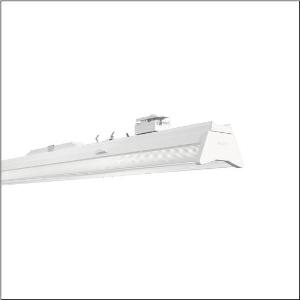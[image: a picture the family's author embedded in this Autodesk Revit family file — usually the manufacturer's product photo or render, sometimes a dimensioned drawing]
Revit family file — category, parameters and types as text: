
# Revit family: licross_r__21_performance_mo_52td167n485g_efc6
name_source: partatom
category: Lighting Fixtures
units: mm (PartAtom-declared; Revit-internal decimal feet)

## family parameters
Cut with Voids When Loaded = No
Host = Face
Light Source = No
Part Type = Normal
Room Calculation Point = No
Round Connector Dimension = Use Diameter
Shared = No

## types (1)
- Licross® 21 Performance MO (1 x LED, 8720 lm, 47.9 W, 4000K)
    Apparent Load = 48 VA
    CIE Flux Codes = 66 88 96 79 100
    Color Rendering = 80
    Color Temperature = 4000K
    Default Elevation = 1800 mm
    Description = Licross® 21 Performance MO, luminaire insert, of sheet steel, galvanised, coil coated, white, length: 1.500mm, width: 120mm, height: 123mm, LED rated luminous flux: 8.720lm, light colour: 840, SDCM (Standard Deviation of Colour Matching)MacAdam ≤ 3 SDCM (initial), control gear: ON/OFF, with plug, 3-pole, with phase selection, mains connection: 220..240V, AC, 50/60Hz, rated input power: 48W, internal wiring halogen-free, primary light control with lens, of plastic, primary optical cover: cover, of PMMA, light emission: direct/indirect distribution, primary light characteristic: symmetric, protection rating (complete): IP54, insulation class (complete): insulation class I (protective earthing), certification: CE, ENEC, UKCA, protection symbol: D if used in an environment with non-conductive dust loads with corresponding accessories, impact resistance: IK06, permissible ambient temperature for indoor applications: -35..+45°C, corresponds to IFS (International Featured Standards) requirements for safety and quality in the food industry, reducing of maximum allowable ambient temperature of 5°C with ceiling mounting, LABS conformity tested according to VDMA 24364:2018-05, packaging unit: 1 piece
    Height = 114 mm
    Lamp = 1 x LED
    Lamp Light Flux = 8720 lm
    Lamp Power = 47.9 W
    Lamp count = 1
    Length = 1500 mm
    Luminous efficacy = 182 lm/W
    Manufacturer = Siteco
    ModVariant = No
    Model = 52TD167N485G
    Mounting Place = Ceiling
    Mounting Type = Pendant
    Number of Poles = 1
    OnlyDefault = Yes
    Power Factor = 1
    Product Name = Licross® 21 Performance MO
    Product group = luminaire insert | ceiling pendant
    ProductGroupID = 901
    Protection Class = Protection class I
    Protection Degree = IP 54
    RLX_Detail_Level = 1
    RLX_Emergency_Light_Flux = 0 lm
    RLX_Emergency_Type = 0
    RLX_Emergency_Type_DB = No
    RlxData = <blob elided: 30457 chars, md5=7da62960>
    Socket = socket
    Standby Power = 0 W
    System Light Flux = 8720 lm
    System Power = 48 W
    Type Comments = Product without accessories
    Type Image = l_1256138.jpg
    URL = http://relux.com
    VarID = ---
    Voltage = 0 V
    Weight = 0.00 kg
    Width = 120 mm

## geometry (parser evidence)
native form markers: Blend x4, Sweep x11
no freeform markers — native parametric forms only
